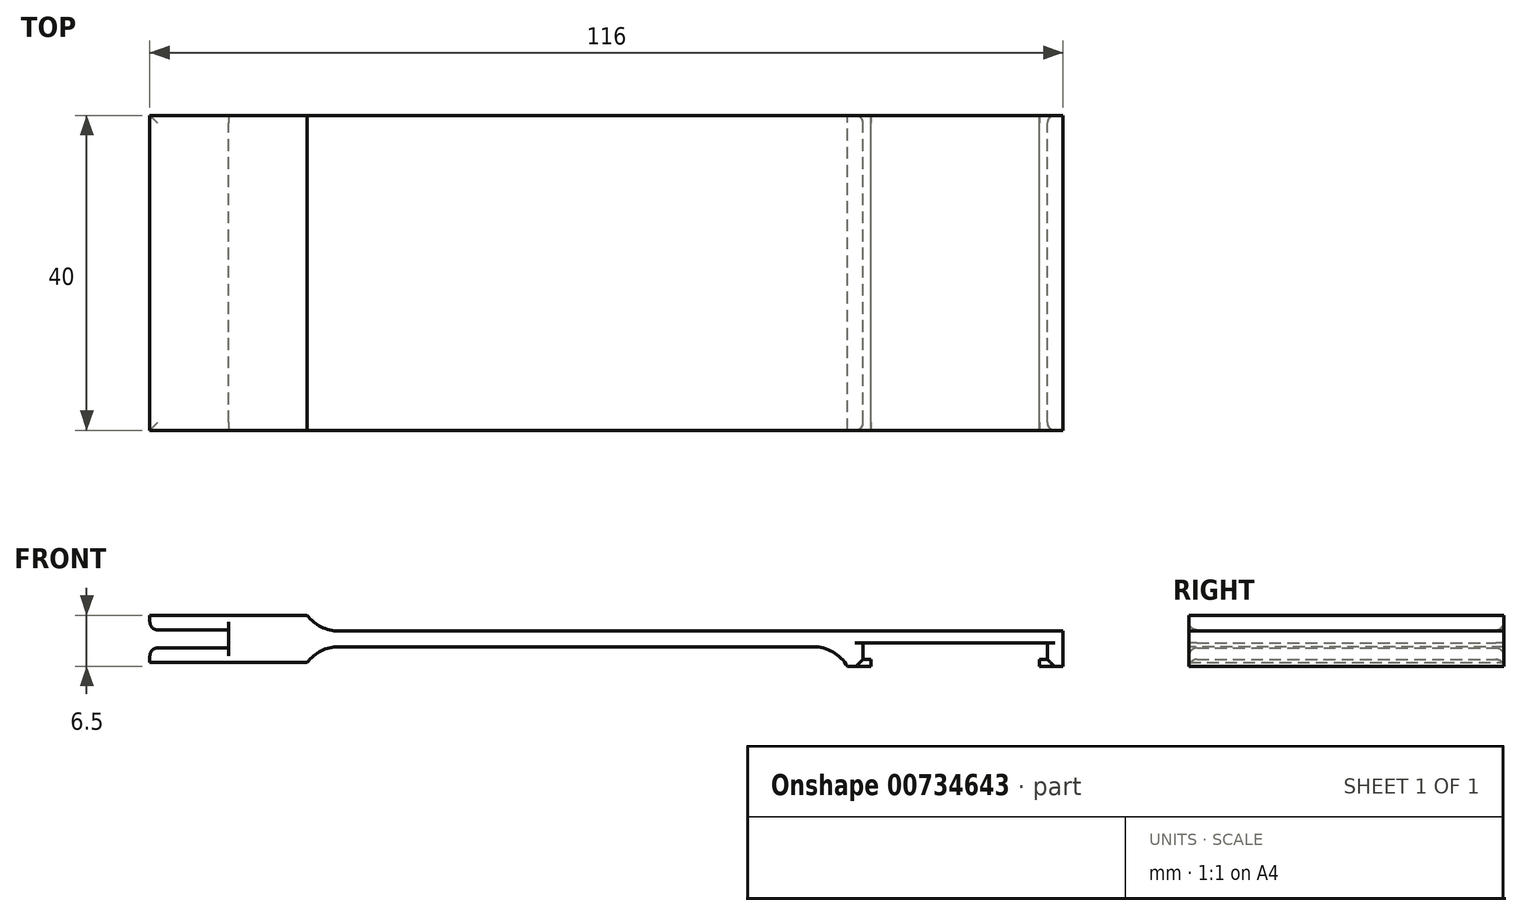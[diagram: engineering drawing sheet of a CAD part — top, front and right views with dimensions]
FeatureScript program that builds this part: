
annotation { "Feature Type Name" : "Feature", "Feature Type Description" : "" }
export const myFeature = defineFeature(function(context is Context, id is Id, definition is map)
    precondition{}
    {
        {
            var Q0;
            Q0=qCreatedBy(makeId("Front.planeOp"),FACE);
            var sketch = newSketch(context, id + "F0", { "sketchPlane" : qUnion([Q0])});
            skLineSegment(sketch, "E0.bottom", {"start": v(10, 0) * mm, "end": v(106, 0) * mm});
            skLineSegment(sketch, "E0.top", {"start": v(10, -2) * mm, "end": v(78.6, -2) * mm});
            skLineSegment(sketch, "E0.left", {"start": v(0, 0) * mm, "end": v(0, -2) * mm});
            skLineSegment(sketch, "E0.right", {"start": v(106, 0) * mm, "end": v(106, -2) * mm});
            skLineSegment(sketch, "E1.top", {"start": v(106, -4.5) * mm, "end": v(103, -4.5) * mm});
            skLineSegment(sketch, "E1.left", {"start": v(106, -2) * mm, "end": v(106, -4.5) * mm});
            skLineSegment(sketch, "E1.right", {"start": v(103, -3.6) * mm, "end": v(103, -4.5) * mm});
            skLineSegment(sketch, "E2", {"start": v(103, -3.6) * mm, "end": v(104, -3.6) * mm});
            skLineSegment(sketch, "E3", {"start": v(104, -3.6) * mm, "end": v(104, -2) * mm});
            skLineSegment(sketch, "E4.top", {"start": v(78.6, -4.5) * mm, "end": v(81.6, -4.5) * mm});
            skLineSegment(sketch, "E4.left", {"start": v(78.6, -2) * mm, "end": v(78.6, -4.5) * mm});
            skLineSegment(sketch, "E4.right", {"start": v(81.6, -3.6) * mm, "end": v(81.6, -4.5) * mm});
            skLineSegment(sketch, "E5", {"start": v(81.6, -3.6) * mm, "end": v(80.6, -3.6) * mm});
            skLineSegment(sketch, "E6", {"start": v(80.6, -3.6) * mm, "end": v(80.6, -2) * mm});
            skLineSegment(sketch, "E7.top", {"start": v(10, 2) * mm, "end": v(-10, 2) * mm});
            skLineSegment(sketch, "E7.left", {"start": v(10, 0) * mm, "end": v(10, 2) * mm});
            skLineSegment(sketch, "E7.right", {"start": v(-10, 0.15) * mm, "end": v(-10, 2) * mm});
            skLineSegment(sketch, "E8.top", {"start": v(10, -4) * mm, "end": v(-10, -4) * mm});
            skLineSegment(sketch, "E8.left", {"start": v(10, -2) * mm, "end": v(10, -4) * mm});
            skLineSegment(sketch, "E8.right", {"start": v(-10, -2.15) * mm, "end": v(-10, -4) * mm});
            skLineSegment(sketch, "E9", {"start": v(-10, -2.15) * mm, "end": v(0, -2.15) * mm});
            skLineSegment(sketch, "E10", {"start": v(0, -2.15) * mm, "end": v(0, -2) * mm});
            skLineSegment(sketch, "E11", {"start": v(0, 0.15) * mm, "end": v(-10, 0.15) * mm});
            skPoint(sketch, "E11.endSnap0", {"position": v(-10, 1) * mm});
            skLineSegment(sketch, "E12", {"start": v(0, 0.15) * mm, "end": v(0, 0) * mm});
            skPoint(sketch, "E13.orphan", {"position": v(-10, 0) * mm});
            skLineSegment(sketch, "E14", {"start": v(80.6, -2) * mm, "end": v(80.6, -1.5) * mm});
            skLineSegment(sketch, "E15", {"start": v(80.6, -1.5) * mm, "end": v(104, -1.5) * mm});
            skLineSegment(sketch, "E16", {"start": v(104, -1.5) * mm, "end": v(104, -2) * mm});
            skSolve(sketch);
        }
        {
            var Q0;
            Q0 = qSketchRegion(id + "F0", true);
            extrude(context, id + "F1", {"entities" : qUnion([Q0]), "depth" : 40 * mm, "offsetDistance" : 25 * mm});
        }
        {
            var Q0;
            Q0=makeQuery(id+"F1.opExtrude","SWEPT_EDGE",EDGE,{"disambiguationData":[OSD([sQuery(id+"F0.wireOp",EDGE,"E0.bottom"),sQuery(id+"F0.wireOp",EDGE,"E7.left")])]});
            var Q1;
            Q1=makeQuery(id+"F1.opExtrude","SWEPT_EDGE",EDGE,{"disambiguationData":[OSD([sQuery(id+"F0.wireOp",EDGE,"E0.top"),sQuery(id+"F0.wireOp",EDGE,"E8.left")])]});
            var Q2;
            Q2=makeQuery(id+"F1.opExtrude","SWEPT_EDGE",EDGE,{"disambiguationData":[OSD([sQuery(id+"F0.wireOp",EDGE,"E0.top"),sQuery(id+"F0.wireOp",EDGE,"E4.left")])]});
            fillet(context, id + "F2", {"entities" : qUnion([Q0, Q1, Q2]), "tangentPropagation" : true, "radius" : 5 * mm, "defaultsChanged" : false, "vertexSettings" : [], "allowEdgeOverflow" : false});
        }
        {
            var Q0;
            Q0=makeQuery(id+"F1.opExtrude","CAP_EDGE",EDGE,{"disambiguationData":[OSD([sQuery(id+"F0.wireOp",EDGE,"E11")])],"isStart":false});
            var Q1;
            Q1=makeQuery(id+"F1.opExtrude","CAP_EDGE",EDGE,{"disambiguationData":[OSD([sQuery(id+"F0.wireOp",EDGE,"E9")])],"isStart":false});
            var Q2;
            Q2=makeQuery(id+"F1.opExtrude","SWEPT_EDGE",EDGE,{"disambiguationData":[OSD([sQuery(id+"F0.wireOp",EDGE,"E7.right"),sQuery(id+"F0.wireOp",EDGE,"E11")])]});
            var Q3;
            Q3=makeQuery(id+"F1.opExtrude","SWEPT_EDGE",EDGE,{"disambiguationData":[OSD([sQuery(id+"F0.wireOp",EDGE,"E8.right"),sQuery(id+"F0.wireOp",EDGE,"E9")])]});
            var Q4;
            Q4=makeQuery(id+"F1.opExtrude","CAP_EDGE",EDGE,{"disambiguationData":[OSD([sQuery(id+"F0.wireOp",EDGE,"E11")])],"isStart":true});
            var Q5;
            Q5=makeQuery(id+"F1.opExtrude","CAP_EDGE",EDGE,{"disambiguationData":[OSD([sQuery(id+"F0.wireOp",EDGE,"E9")])],"isStart":true});
            var Q6;
            Q6=makeQuery(id+"F1.opExtrude","CAP_EDGE",EDGE,{"disambiguationData":[OSD([sQuery(id+"F0.wireOp",EDGE,"E6")])],"isStart":true});
            var Q7;
            Q7=makeQuery(id+"F1.opExtrude","CAP_EDGE",EDGE,{"disambiguationData":[OSD([sQuery(id+"F0.wireOp",EDGE,"E3")])],"isStart":true});
            var Q8;
            Q8=makeQuery(id+"F1.opExtrude","CAP_EDGE",EDGE,{"disambiguationData":[OSD([sQuery(id+"F0.wireOp",EDGE,"E6")])],"isStart":false});
            var Q9;
            Q9=makeQuery(id+"F1.opExtrude","CAP_EDGE",EDGE,{"disambiguationData":[OSD([sQuery(id+"F0.wireOp",EDGE,"E3")])],"isStart":false});
            var Q10;
            Q10=makeQuery(id+"F1.opExtrude","CAP_EDGE",EDGE,{"disambiguationData":[OSD([sQuery(id+"F0.wireOp",EDGE,"E5")])],"isStart":false});
            var Q11;
            Q11=makeQuery(id+"F1.opExtrude","CAP_EDGE",EDGE,{"disambiguationData":[OSD([sQuery(id+"F0.wireOp",EDGE,"E2")])],"isStart":false});
            var Q12;
            Q12=makeQuery(id+"F1.opExtrude","CAP_EDGE",EDGE,{"disambiguationData":[OSD([sQuery(id+"F0.wireOp",EDGE,"E2")])],"isStart":true});
            var Q13;
            Q13=makeQuery(id+"F1.opExtrude","CAP_EDGE",EDGE,{"disambiguationData":[OSD([sQuery(id+"F0.wireOp",EDGE,"E5")])],"isStart":true});
            fillet(context, id + "F3", {"entities" : qUnion([Q0, Q1, Q2, Q3, Q4, Q5, Q6, Q7, Q8, Q9, Q10, Q11, Q12, Q13]), "tangentPropagation" : true, "radius" : 1 * mm, "defaultsChanged" : false, "vertexSettings" : [], "allowEdgeOverflow" : false});
        }
    });
